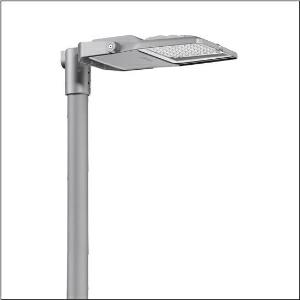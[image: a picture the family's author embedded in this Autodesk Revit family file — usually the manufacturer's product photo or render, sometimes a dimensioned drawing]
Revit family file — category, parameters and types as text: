
# Revit family: floodlight_fl_21_iq_mini___pl52_5xa7771d4d3a_bc98
name_source: partatom
category: Lighting Fixtures
units: mm (PartAtom-declared; Revit-internal decimal feet)

## family parameters
Cut with Voids When Loaded = No
Host = Face
Light Source = No
Part Type = Normal
Room Calculation Point = No
Round Connector Dimension = Use Diameter
Shared = No

## types (1)
- --- (1 x LED, 18610 lm, 143 W, 4000K)
    Apparent Load = 143 VA
    CIE Flux Codes = 26 60 98 100 100
    Color Rendering = 70
    Color Temperature = 4000K
    Default Elevation = 1800 mm
    Description = Floodlight FL 21 iQ mini, floodlight, primary light control with lens, of PMMA, primary optical cover: protective disc, of toughened safety glass, transparent, light distribution: PL52, light emission: direct distribution, installation type: surface-mounted, LED, High Power LED, rated luminous flux: 18.610lm, luminous efficacy: 130lm/W, light colour: 740, colour temperature: 4000K, control: Auto-Match, Temp-Guard, Lumen-Switch, Night-Set, Smart-Wire, Light-Fading, Desk-Remote (wireless, voltage-free reading and setting of iQ features in the workshop via application-optimized NFC function/RFID function), optimised constant luminous flux control (CLO 2.0), with terminal, 6-pole, mains connection: 220..240V, AC, 50/60Hz, start of lifetime: 143W, end of service life: 152W, reduction: 61W, luminaire housing, of diecast aluminium, powder-coated, Siteco® metallic grey (DB 702S), corrosivity category C5 mid according to DIN EN ISO 12944, sealing non-destructively replaceable, please order mast flange separately, mast bracket, of steel, galvanised, powder-coated, Siteco® metallic grey (DB 702S), protection rating (complete): IP66, insulation class (complete): insulation class II (safety insulation), certification: CE, ENEC, VDE, protection symbol: D, impact resistance: IK08, permissible operating ambient temperature: -40..+40°C, permissible operating ambient temperature for outdoor applications: -40..+50°C, standard: DIN EN 12944, LABS conformity tested according to VDMA 24364:2018-05, packaging unit: 1 piece

Light Distribution: PL52
    Height = 70 mm
    Lamp = 1 x LED
    Lamp Light Flux = 18610 lm
    Lamp Power = 143 W
    Lamp count = 1
    Length = 485 mm
    Luminous efficacy = 130 lm/W
    Manufacturer = Siteco
    ModVariant = No
    Model = 5XA7771D4D3A
    Number of Poles = 1
    OnlyDefault = Yes
    Power Factor = 1
    Product Name = Floodlight FL 21 iQ mini | PL52
    Product group = floodlight | pylon annexe
    ProductGroupID = 6200
    Protection Class = Protection class II
    Protection Degree = IP 66
    RLX_Detail_Level = 1
    RLX_Emergency_Light_Flux = 0 lm
    RLX_Emergency_Type = 0
    RLX_Emergency_Type_DB = No
    RlxData = <blob elided: 101893 chars, md5=e9ceec9c>
    Socket = socket
    Standby Power = 0 W
    System Light Flux = 18610 lm
    System Power = 143 W
    Type Comments = factory setting: luminous flux: 100 % | dim-lin: 254 | 730 mA
    Type Image = l_1007125.jpg
    URL = http://relux.com
    VarID = @adj_114015
    Voltage = 0 V
    Weight = 0.00 kg
    Width = 337 mm

## geometry (parser evidence)
native form markers: Blend x4, Sweep x11
no freeform markers — native parametric forms only
